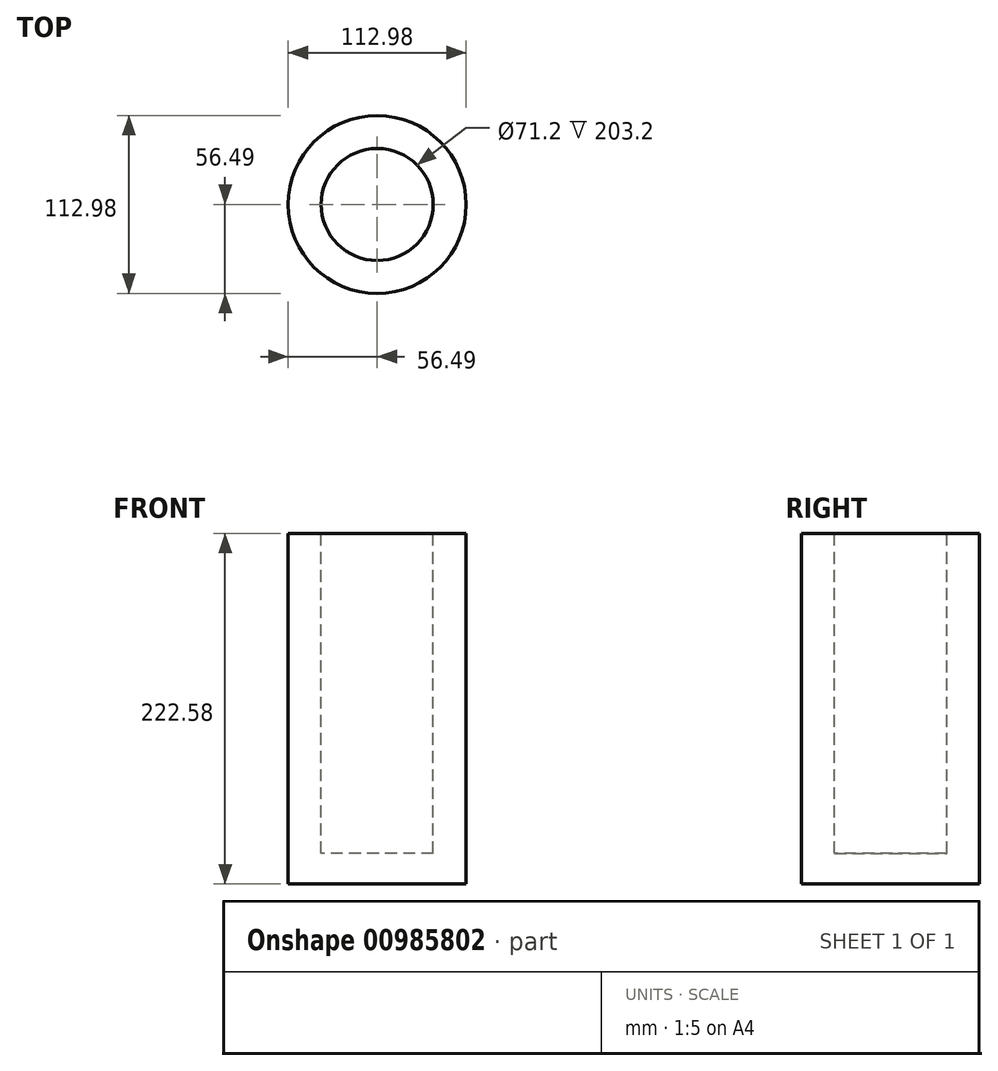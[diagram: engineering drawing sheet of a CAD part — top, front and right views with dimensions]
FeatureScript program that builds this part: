
annotation { "Feature Type Name" : "Feature", "Feature Type Description" : "" }
export const myFeature = defineFeature(function(context is Context, id is Id, definition is map)
    precondition{}
    {
        {
            var Q0;
            Q0=qCreatedBy(makeId("Top.planeOp"),FACE);
            var sketch = newSketch(context, id + "F0", { "sketchPlane" : qUnion([Q0])});
            skCircle(sketch, "E0", {"center": v(0, 0) * mm, "radius": 56.5 * mm});
            skSolve(sketch);
        }
        {
            var Q0;
            Q0=makeQuery(id+"F0.imprint","IMPRINT",FACE,{"disambiguationData":[TD([[makeQuery(id+"F0.imprint","IMPRINT",EDGE,{"derivedFrom":sQuery(id+"F0.wireOp",EDGE,"E0")}),1.0]])]});
            var Q1;
            Q1=sQuery(id+"F0.wireOp",EDGE,"E0");
            extrude(context, id + "F1", {"entities" : qUnion([Q0]), "surfaceEntities" : qUnion([Q1]), "depth" : 154.94 * mm, "offsetDistance" : 25.4 * mm});
        }
        {
            var Q0;
            Q0=makeQuery(id+"F1.opExtrude","CAP_FACE",FACE,{"disambiguationData":[OSD([sQuery(id+"F0.wireOp",EDGE,"E0")])],"isStart":false});
            extrude(context, id + "F2", {"entities" : qUnion([Q0]), "operationType" : NewBodyOperationType.ADD, "endBound" : BoundingType.UP_TO_NEXT, "oppositeDirection" : true, "depth" : 25.4 * mm, "offsetDistance" : 25.4 * mm});
        }
        {
            var Q0;
            Q0=makeQuery(id+"F1.opExtrude","CAP_FACE",FACE,{"disambiguationData":[OSD([sQuery(id+"F0.wireOp",EDGE,"E0")])],"isStart":false});
            extrude(context, id + "F3", {"entities" : qUnion([Q0]), "operationType" : NewBodyOperationType.ADD, "endBound" : BoundingType.THROUGH_ALL, "oppositeDirection" : true, "depth" : 25.4 * mm, "offsetDistance" : 25.4 * mm});
        }
        {
            var Q0;
            Q0=makeQuery(id+"F1.opExtrude","CAP_FACE",FACE,{"disambiguationData":[OSD([sQuery(id+"F0.wireOp",EDGE,"E0")])],"isStart":false});
            var sketch = newSketch(context, id + "F4", { "sketchPlane" : qUnion([Q0])});
            skCircle(sketch, "E1", {"center": v(0, 0) * mm, "radius": 35.6 * mm});
            skSolve(sketch);
        }
        {
            var Q0;
            Q0=makeQuery(id+"F4.imprint","IMPRINT",FACE,{"disambiguationData":[TD([[makeQuery(id+"F4.imprint","IMPRINT",EDGE,{"derivedFrom":sQuery(id+"F4.wireOp",EDGE,"E1")}),1.0]])]});
            extrude(context, id + "F5", {"entities" : qUnion([Q0]), "operationType" : NewBodyOperationType.REMOVE, "oppositeDirection" : true, "depth" : 203.2 * mm, "offsetDistance" : 25.4 * mm});
        }
    });
